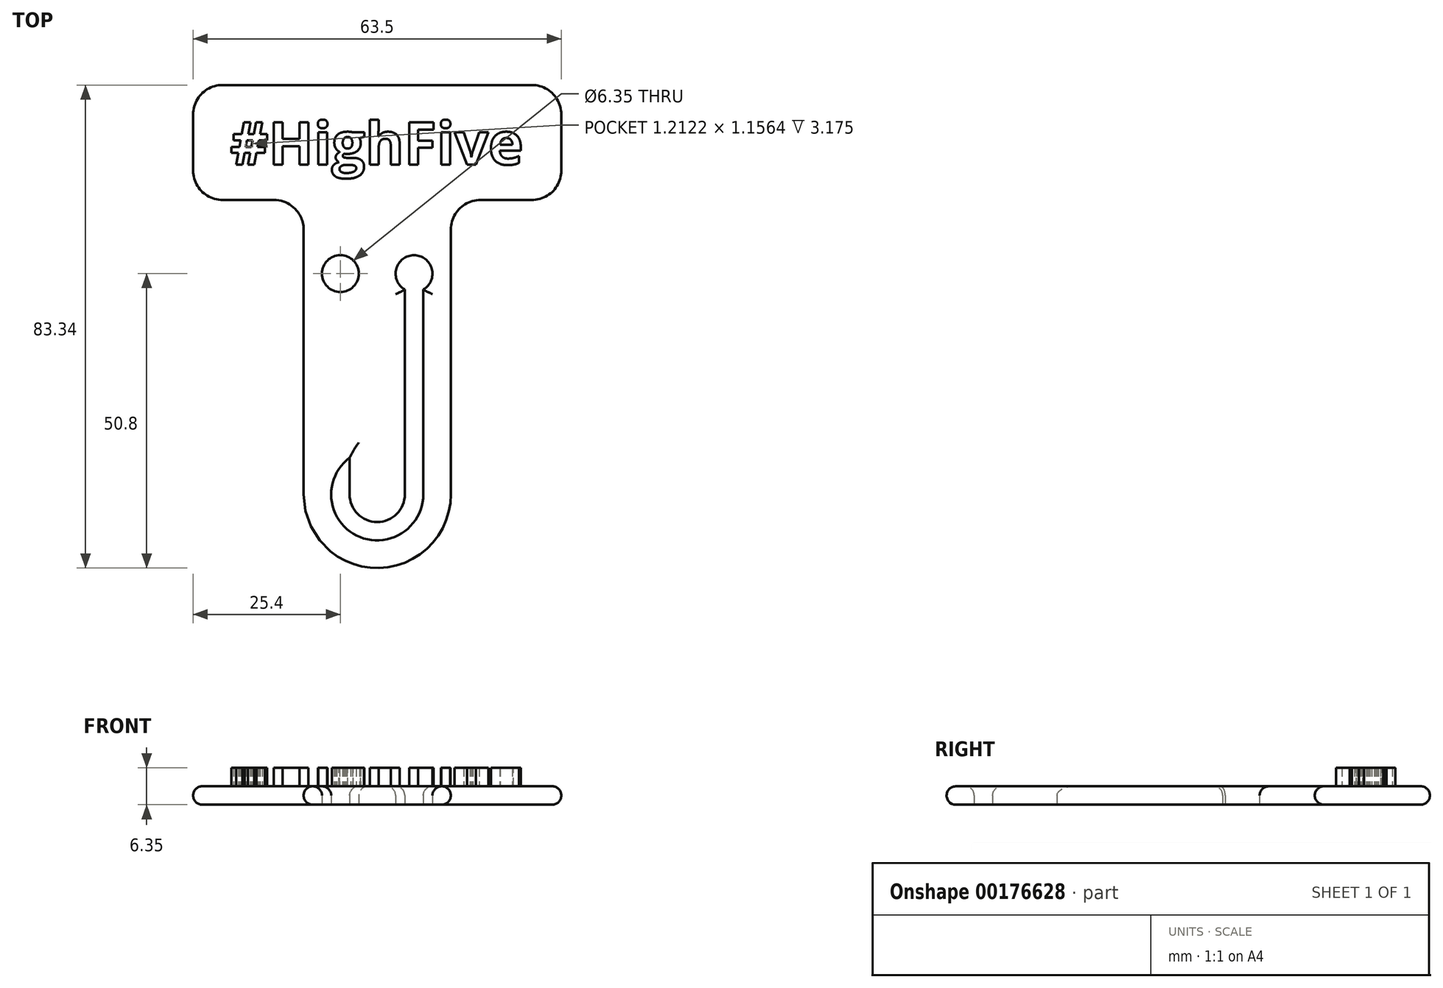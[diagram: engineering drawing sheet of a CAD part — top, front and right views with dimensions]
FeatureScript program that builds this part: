
annotation { "Feature Type Name" : "Feature", "Feature Type Description" : "" }
export const myFeature = defineFeature(function(context is Context, id is Id, definition is map)
    precondition{}
    {
        {
            var Q0;
            Q0=qCreatedBy(makeId("Top.planeOp"),FACE);
            var sketch = newSketch(context, id + "F0", { "sketchPlane" : qUnion([Q0])});
            skLineSegment(sketch, "E0", {"start": v(0, 0) * mm, "end": v(0, -50.8) * mm, "construction": true});
            skLineSegment(sketch, "E1", {"start": v(0, -50.8) * mm, "end": v(0, -63.5) * mm, "construction": true});
            skLineSegment(sketch, "E2.bottom", {"start": v(12.7, 0) * mm, "end": v(-12.7, 0) * mm});
            skLineSegment(sketch, "E2.top", {"start": v(12.7, -50.8) * mm, "end": v(-12.7, -50.8) * mm});
            skLineSegment(sketch, "E2.left", {"start": v(12.7, 0) * mm, "end": v(12.7, -50.8) * mm});
            skLineSegment(sketch, "E2.right", {"start": v(-12.7, 0) * mm, "end": v(-12.7, -50.8) * mm});
            skPoint(sketch, "E2.middle", {"position": v(0, -25.4) * mm});
            skLineSegment(sketch, "E3", {"start": v(0, 0) * mm, "end": v(0, 9.92) * mm, "construction": true});
            skLineSegment(sketch, "E4.bottom", {"start": v(31.75, 0) * mm, "end": v(-31.75, 0) * mm});
            skLineSegment(sketch, "E4.top", {"start": v(31.75, 19.84) * mm, "end": v(-31.75, 19.84) * mm});
            skLineSegment(sketch, "E4.left", {"start": v(31.75, 0) * mm, "end": v(31.75, 19.84) * mm});
            skLineSegment(sketch, "E4.right", {"start": v(-31.75, 0) * mm, "end": v(-31.75, 19.84) * mm});
            skPoint(sketch, "E4.middle", {"position": v(0, 9.92) * mm});
            skArc(sketch, "E5", {"start": v(-12.7, -50.8) * mm, "mid": v(0, -63.5) * mm, "end": v(12.7, -50.8) * mm});
            skText(sketch, "E6", { "text": "#HighFive", "fontName": "OpenSans-Bold.ttf"});
            const initialGuessF0  = {"E6": [-0.02537, 0.00611, 1, 0, 0.00735]};
            skSetInitialGuess(sketch, initialGuessF0);
            skSolve(sketch);
        }
        {
            var Q0;
            Q0=makeQuery(id+"F0.imprint","IMPRINT",FACE,{"disambiguationData":[TD([[makeQuery(id+"F0.imprint","IMPRINT",EDGE,{"derivedFrom":sQuery(id+"F0.wireOp",EDGE,"E2.top")}),1.0]])]});
            var Q1;
            Q1=makeQuery(id+"F0.imprint","IMPRINT",FACE,{"disambiguationData":[TD([[makeQuery(id+"F0.imprint","IMPRINT",EDGE,{"derivedFrom":sQuery(id+"F0.wireOp",EDGE,"E2.top")}),-1.0]])]});
            var Q2;
            Q2=makeQuery(id+"F0.imprint","IMPRINT",FACE,{"disambiguationData":[TD([[makeQuery(id+"F0.imprint","IMPRINT",EDGE,{"derivedFrom":sQuery(id+"F0.wireOp",EDGE,"E4.top")}),1.0]])]});
            var Q3;
            Q3=makeQuery(id+"F0.imprint","IMPRINT",FACE,{"disambiguationData":[TD([[makeQuery(id+"F0.imprint","IMPRINT",EDGE,{"derivedFrom":sQuery(id+"F0.wireOp",EDGE,"E6.sketch_text.stroke-82")}),1.0]])]});
            var Q4;
            Q4=makeQuery(id+"F0.imprint","IMPRINT",FACE,{"disambiguationData":[TD([[makeQuery(id+"F0.imprint","IMPRINT",EDGE,{"derivedFrom":sQuery(id+"F0.wireOp",EDGE,"E6.sketch_text.stroke-91")}),1.0]])]});
            var Q5;
            Q5=makeQuery(id+"F0.imprint","IMPRINT",FACE,{"disambiguationData":[TD([[makeQuery(id+"F0.imprint","IMPRINT",EDGE,{"derivedFrom":sQuery(id+"F0.wireOp",EDGE,"E6.sketch_text.stroke-28")}),1.0]])]});
            var Q6;
            Q6=makeQuery(id+"F0.imprint","IMPRINT",FACE,{"disambiguationData":[TD([[makeQuery(id+"F0.imprint","IMPRINT",EDGE,{"derivedFrom":sQuery(id+"F0.wireOp",EDGE,"E6.sketch_text.stroke-143")}),1.0]])]});
            extrude(context, id + "F1", {"entities" : qUnion([Q0, Q1, Q2, Q3, Q4, Q5, Q6]), "depth" : 3.17 * mm});
        }
        {
            var Q0;
            Q0=makeQuery(id+"F0.imprint","IMPRINT",FACE,{"disambiguationData":[TD([[makeQuery(id+"F0.imprint","IMPRINT",EDGE,{"derivedFrom":sQuery(id+"F0.wireOp",EDGE,"E6.sketch_text.stroke-32")}),-1.0]])]});
            var Q1;
            Q1=makeQuery(id+"F0.imprint","IMPRINT",FACE,{"disambiguationData":[TD([[makeQuery(id+"F0.imprint","IMPRINT",EDGE,{"derivedFrom":sQuery(id+"F0.wireOp",EDGE,"E6.sketch_text.stroke-0")}),-1.0]])]});
            var Q2;
            Q2=makeQuery(id+"F0.imprint","IMPRINT",FACE,{"disambiguationData":[TD([[makeQuery(id+"F0.imprint","IMPRINT",EDGE,{"derivedFrom":sQuery(id+"F0.wireOp",EDGE,"E6.sketch_text.stroke-49")}),-1.0]])]});
            var Q3;
            Q3=makeQuery(id+"F0.imprint","IMPRINT",FACE,{"disambiguationData":[TD([[makeQuery(id+"F0.imprint","IMPRINT",EDGE,{"derivedFrom":sQuery(id+"F0.wireOp",EDGE,"E6.sketch_text.stroke-53")}),-1.0]])]});
            var Q4;
            Q4=makeQuery(id+"F0.imprint","IMPRINT",FACE,{"disambiguationData":[TD([[makeQuery(id+"F0.imprint","IMPRINT",EDGE,{"derivedFrom":sQuery(id+"F0.wireOp",EDGE,"E6.sketch_text.stroke-97")}),-1.0]])]});
            var Q5;
            Q5=makeQuery(id+"F0.imprint","IMPRINT",FACE,{"disambiguationData":[TD([[makeQuery(id+"F0.imprint","IMPRINT",EDGE,{"derivedFrom":sQuery(id+"F0.wireOp",EDGE,"E6.sketch_text.stroke-114")}),-1.0]])]});
            var Q6;
            Q6=makeQuery(id+"F0.imprint","IMPRINT",FACE,{"disambiguationData":[TD([[makeQuery(id+"F0.imprint","IMPRINT",EDGE,{"derivedFrom":sQuery(id+"F0.wireOp",EDGE,"E6.sketch_text.stroke-44")}),-1.0]])]});
            var Q7;
            Q7=makeQuery(id+"F0.imprint","IMPRINT",FACE,{"disambiguationData":[TD([[makeQuery(id+"F0.imprint","IMPRINT",EDGE,{"derivedFrom":sQuery(id+"F0.wireOp",EDGE,"E6.sketch_text.stroke-124")}),-1.0]])]});
            var Q8;
            Q8=makeQuery(id+"F0.imprint","IMPRINT",FACE,{"disambiguationData":[TD([[makeQuery(id+"F0.imprint","IMPRINT",EDGE,{"derivedFrom":sQuery(id+"F0.wireOp",EDGE,"E6.sketch_text.stroke-129")}),-1.0]])]});
            var Q9;
            Q9=makeQuery(id+"F0.imprint","IMPRINT",FACE,{"disambiguationData":[TD([[makeQuery(id+"F0.imprint","IMPRINT",EDGE,{"derivedFrom":sQuery(id+"F0.wireOp",EDGE,"E6.sketch_text.stroke-133")}),-1.0]])]});
            var Q10;
            Q10=makeQuery(id+"F0.imprint","IMPRINT",FACE,{"disambiguationData":[TD([[makeQuery(id+"F0.imprint","IMPRINT",EDGE,{"derivedFrom":sQuery(id+"F0.wireOp",EDGE,"E6.sketch_text.stroke-143")}),-1.0]])]});
            extrude(context, id + "F2", {"entities" : qUnion([Q0, Q1, Q2, Q3, Q4, Q5, Q6, Q7, Q8, Q9, Q10]), "operationType" : NewBodyOperationType.ADD, "depth" : 6.35 * mm});
        }
        {
            var Q0;
            Q0=qCreatedBy(makeId("Top.planeOp"),FACE);
            var sketch = newSketch(context, id + "F3", { "sketchPlane" : qUnion([Q0])});
            skLineSegment(sketch, "E7", {"start": v(0, 0) * mm, "end": v(0, -50.8) * mm, "construction": true});
            skLineSegment(sketch, "E8", {"start": v(0, -50.8) * mm, "end": v(6.35, -50.8) * mm, "construction": true});
            skLineSegment(sketch, "E9", {"start": v(6.35, -50.8) * mm, "end": v(6.35, -12.7) * mm, "construction": true});
            skCircle(sketch, "E10", {"center": v(6.35, -12.7) * mm, "radius": 3.18 * mm});
            skCircle(sketch, "E11.MirrorC", {"center": v(-6.35, -12.7) * mm, "radius": 3.18 * mm});
            skLineSegment(sketch, "E12.MirrorCS", {"start": v(-6.35, -50.8) * mm, "end": v(-6.35, -12.7) * mm, "construction": true});
            skLineSegment(sketch, "E13.bottom", {"start": v(-4.76, -50.8) * mm, "end": v(-7.94, -50.8) * mm});
            skLineSegment(sketch, "E13.top", {"start": v(-4.76, -12.7) * mm, "end": v(-7.94, -12.7) * mm});
            skLineSegment(sketch, "E13.left", {"start": v(-4.76, -50.8) * mm, "end": v(-4.76, -12.7) * mm});
            skLineSegment(sketch, "E13.right", {"start": v(-7.94, -50.8) * mm, "end": v(-7.94, -12.7) * mm});
            skPoint(sketch, "E13.middle", {"position": v(-6.35, -31.75) * mm});
            skLineSegment(sketch, "E14.bottom", {"start": v(7.94, -50.8) * mm, "end": v(4.76, -50.8) * mm});
            skLineSegment(sketch, "E14.top", {"start": v(7.94, -12.7) * mm, "end": v(4.76, -12.7) * mm});
            skLineSegment(sketch, "E14.left", {"start": v(7.94, -50.8) * mm, "end": v(7.94, -12.7) * mm});
            skLineSegment(sketch, "E14.right", {"start": v(4.76, -50.8) * mm, "end": v(4.76, -12.7) * mm});
            skPoint(sketch, "E14.middle", {"position": v(6.35, -31.75) * mm});
            skCircle(sketch, "E15", {"center": v(0, -50.8) * mm, "radius": 4.76 * mm});
            skCircle(sketch, "E16", {"center": v(0, -50.8) * mm, "radius": 7.94 * mm});
            skSolve(sketch);
        }
        {
            var Q0;
            {var subQ5=sQuery(id+"F3.wireOp",EDGE,"E13.top");Q0=makeQuery(id+"F3.imprint","IMPRINT",FACE,{"disambiguationData":[TD([[makeQuery(id+"F3.imprint","IMPRINT",EDGE,{"derivedFrom":subQ5}),-1.0]])]});}
            var Q1;
            {var subQ5=sQuery(id+"F3.wireOp",EDGE,"E13.top");Q1=makeQuery(id+"F3.imprint","IMPRINT",FACE,{"disambiguationData":[TD([[makeQuery(id+"F3.imprint","IMPRINT",EDGE,{"derivedFrom":subQ5}),1.0]])]});}
            var Q2;
            {var subQ0=sQuery(id+"F3.wireOp",EDGE,"E13.left");var subQ1=sQuery(id+"F3.wireOp",EDGE,"E11.MirrorC");var subQ2=makeQuery(id+"F3.imprint","INTERSECT",VERTEX,{"derivedFrom":[subQ1,subQ0]});Q2=makeQuery(id+"F3.imprint","IMPRINT",FACE,{"disambiguationData":[TD([[makeQuery(id+"F3.imprint","IMPRINT",EDGE,{"disambiguationData":[TD([[subQ2,-1.0]])],"derivedFrom":subQ1}),1.0]])]});}
            var Q3;
            {var subQ0=sQuery(id+"F3.wireOp",EDGE,"E13.bottom");Q3=makeQuery(id+"F3.imprint","IMPRINT",FACE,{"disambiguationData":[TD([[makeQuery(id+"F3.imprint","IMPRINT",EDGE,{"derivedFrom":subQ0}),-1.0]])]});}
            var Q4;
            {var subQ0=sQuery(id+"F3.wireOp",EDGE,"E13.bottom");Q4=makeQuery(id+"F3.imprint","IMPRINT",FACE,{"disambiguationData":[TD([[makeQuery(id+"F3.imprint","IMPRINT",EDGE,{"derivedFrom":subQ0}),1.0]])]});}
            var Q5;
            {var subQ0=sQuery(id+"F3.wireOp",EDGE,"E14.bottom");Q5=makeQuery(id+"F3.imprint","IMPRINT",FACE,{"disambiguationData":[TD([[makeQuery(id+"F3.imprint","IMPRINT",EDGE,{"derivedFrom":subQ0}),-1.0]])]});}
            var Q6;
            {var subQ0=sQuery(id+"F3.wireOp",EDGE,"E14.left");var subQ1=sQuery(id+"F3.wireOp",EDGE,"E10");var subQ2=makeQuery(id+"F3.imprint","INTERSECT",VERTEX,{"derivedFrom":[subQ1,subQ0]});Q6=makeQuery(id+"F3.imprint","IMPRINT",FACE,{"disambiguationData":[TD([[makeQuery(id+"F3.imprint","IMPRINT",EDGE,{"disambiguationData":[TD([[subQ2,1.0]])],"derivedFrom":subQ1}),-1.0]])]});}
            var Q7;
            {var subQ5=sQuery(id+"F3.wireOp",EDGE,"E14.top");Q7=makeQuery(id+"F3.imprint","IMPRINT",FACE,{"disambiguationData":[TD([[makeQuery(id+"F3.imprint","IMPRINT",EDGE,{"derivedFrom":subQ5}),-1.0]])]});}
            var Q8;
            {var subQ5=sQuery(id+"F3.wireOp",EDGE,"E14.top");Q8=makeQuery(id+"F3.imprint","IMPRINT",FACE,{"disambiguationData":[TD([[makeQuery(id+"F3.imprint","IMPRINT",EDGE,{"derivedFrom":subQ5}),1.0]])]});}
            extrude(context, id + "F4", {"entities" : qUnion([Q0, Q1, Q2, Q3, Q4, Q5, Q6, Q7, Q8]), "operationType" : NewBodyOperationType.REMOVE, "depth" : 25.4 * mm});
        }
        {
            var Q0;
            Q0=makeQuery(id+"F1.opExtrude","SWEPT_EDGE",EDGE,{"disambiguationData":[OSD([sQuery(id+"F0.wireOp",EDGE,"E4.top"),sQuery(id+"F0.wireOp",EDGE,"E4.right")])]});
            var Q1;
            Q1=makeQuery(id+"F1.opExtrude","SWEPT_EDGE",EDGE,{"disambiguationData":[OSD([sQuery(id+"F0.wireOp",EDGE,"E4.top"),sQuery(id+"F0.wireOp",EDGE,"E4.left")])]});
            var Q2;
            Q2=makeQuery(id+"F1.opExtrude","SWEPT_EDGE",EDGE,{"disambiguationData":[OSD([sQuery(id+"F0.wireOp",EDGE,"E4.bottom"),sQuery(id+"F0.wireOp",EDGE,"E4.left")])]});
            var Q3;
            Q3=makeQuery(id+"F1.opExtrude","SWEPT_EDGE",EDGE,{"disambiguationData":[OSD([sQuery(id+"F0.wireOp",EDGE,"E4.bottom"),sQuery(id+"F0.wireOp",EDGE,"E4.right")])]});
            var Q4;
            Q4=makeQuery(id+"F1.opExtrude","SWEPT_EDGE",EDGE,{"disambiguationData":[OSD([sQuery(id+"F0.wireOp",EDGE,"E2.right"),sQuery(id+"F0.wireOp",EDGE,"E4.bottom")])]});
            var Q5;
            Q5=makeQuery(id+"F1.opExtrude","SWEPT_EDGE",EDGE,{"disambiguationData":[OSD([sQuery(id+"F0.wireOp",EDGE,"E2.left"),sQuery(id+"F0.wireOp",EDGE,"E4.bottom")])]});
            fillet(context, id + "F5", {"entities" : qUnion([Q0, Q1, Q2, Q3, Q4, Q5]), "radius" : 5.08 * mm, "tangentPropagation" : true, "allowEdgeOverflow" : false});
        }
        {
            var Q0;
            Q0=makeQuery(id+"F1.opExtrude","CAP_EDGE",EDGE,{"disambiguationData":[OSD([sQuery(id+"F0.wireOp",EDGE,"E2.left")])],"isStart":false});
            var Q1;
            {var subQ0=sQuery(id+"F0.wireOp",EDGE,"E4.bottom");Q1=makeQuery(id+"F1.opExtrude","CAP_EDGE",EDGE,{"disambiguationData":[OSD([subQ0]),TDD([makeQuery(id+"F0.imprint","IMPRINT",EDGE,{"disambiguationData":[TD([[makeQuery(id+"F0.imprint","INTERSECT",VERTEX,{"derivedFrom":[sQuery(id+"F0.wireOp",EDGE,"E2.left"),subQ0]}),1.0]])],"derivedFrom":subQ0})])],"isStart":false});}
            var Q2;
            Q2=makeQuery(id+"F1.opExtrude","CAP_EDGE",EDGE,{"disambiguationData":[OSD([sQuery(id+"F0.wireOp",EDGE,"E4.left")])],"isStart":false});
            var Q3;
            {var subQ0=sQuery(id+"F0.wireOp",EDGE,"E4.bottom");Q3=makeQuery(id+"F1.opExtrude","CAP_EDGE",EDGE,{"disambiguationData":[OSD([subQ0]),TDD([makeQuery(id+"F0.imprint","IMPRINT",EDGE,{"disambiguationData":[TD([[makeQuery(id+"F0.imprint","INTERSECT",VERTEX,{"derivedFrom":[sQuery(id+"F0.wireOp",EDGE,"E2.right"),subQ0]}),-1.0]])],"derivedFrom":subQ0})])],"isStart":false});}
            var Q4;
            Q4=makeQuery(id+"F1.opExtrude","CAP_EDGE",EDGE,{"disambiguationData":[OSD([sQuery(id+"F0.wireOp",EDGE,"E4.right")])],"isStart":false});
            var Q5;
            Q5=makeQuery(id+"F1.opExtrude","CAP_EDGE",EDGE,{"disambiguationData":[OSD([sQuery(id+"F0.wireOp",EDGE,"E4.top")])],"isStart":false});
            var Q6;
            Q6=makeQuery(id+"F4.boolean.opBoolean","INTERSECT",EDGE,{"derivedFrom":[makeQuery(id+"F1.opExtrude","CAP_FACE",FACE,{"disambiguationData":[OSD([sQuery(id+"F0.wireOp",EDGE,"E2.left"),sQuery(id+"F0.wireOp",EDGE,"E2.right"),sQuery(id+"F0.wireOp",EDGE,"E4.bottom"),sQuery(id+"F0.wireOp",EDGE,"E4.top"),sQuery(id+"F0.wireOp",EDGE,"E4.left"),sQuery(id+"F0.wireOp",EDGE,"E4.right"),sQuery(id+"F0.wireOp",EDGE,"E5"),sQuery(id+"F0.wireOp",EDGE,"E6.sketch_text.stroke-0"),sQuery(id+"F0.wireOp",EDGE,"E6.sketch_text.stroke-1"),sQuery(id+"F0.wireOp",EDGE,"E6.sketch_text.stroke-2"),sQuery(id+"F0.wireOp",EDGE,"E6.sketch_text.stroke-3"),sQuery(id+"F0.wireOp",EDGE,"E6.sketch_text.stroke-4"),sQuery(id+"F0.wireOp",EDGE,"E6.sketch_text.stroke-5"),sQuery(id+"F0.wireOp",EDGE,"E6.sketch_text.stroke-6"),sQuery(id+"F0.wireOp",EDGE,"E6.sketch_text.stroke-7"),sQuery(id+"F0.wireOp",EDGE,"E6.sketch_text.stroke-8"),sQuery(id+"F0.wireOp",EDGE,"E6.sketch_text.stroke-9"),sQuery(id+"F0.wireOp",EDGE,"E6.sketch_text.stroke-10"),sQuery(id+"F0.wireOp",EDGE,"E6.sketch_text.stroke-11"),sQuery(id+"F0.wireOp",EDGE,"E6.sketch_text.stroke-12"),sQuery(id+"F0.wireOp",EDGE,"E6.sketch_text.stroke-13"),sQuery(id+"F0.wireOp",EDGE,"E6.sketch_text.stroke-14"),sQuery(id+"F0.wireOp",EDGE,"E6.sketch_text.stroke-15"),sQuery(id+"F0.wireOp",EDGE,"E6.sketch_text.stroke-16"),sQuery(id+"F0.wireOp",EDGE,"E6.sketch_text.stroke-17"),sQuery(id+"F0.wireOp",EDGE,"E6.sketch_text.stroke-18"),sQuery(id+"F0.wireOp",EDGE,"E6.sketch_text.stroke-19"),sQuery(id+"F0.wireOp",EDGE,"E6.sketch_text.stroke-20"),sQuery(id+"F0.wireOp",EDGE,"E6.sketch_text.stroke-21"),sQuery(id+"F0.wireOp",EDGE,"E6.sketch_text.stroke-22"),sQuery(id+"F0.wireOp",EDGE,"E6.sketch_text.stroke-23"),sQuery(id+"F0.wireOp",EDGE,"E6.sketch_text.stroke-24"),sQuery(id+"F0.wireOp",EDGE,"E6.sketch_text.stroke-25"),sQuery(id+"F0.wireOp",EDGE,"E6.sketch_text.stroke-26"),sQuery(id+"F0.wireOp",EDGE,"E6.sketch_text.stroke-27"),sQuery(id+"F0.wireOp",EDGE,"E6.sketch_text.stroke-32"),sQuery(id+"F0.wireOp",EDGE,"E6.sketch_text.stroke-33"),sQuery(id+"F0.wireOp",EDGE,"E6.sketch_text.stroke-34"),sQuery(id+"F0.wireOp",EDGE,"E6.sketch_text.stroke-35"),sQuery(id+"F0.wireOp",EDGE,"E6.sketch_text.stroke-36"),sQuery(id+"F0.wireOp",EDGE,"E6.sketch_text.stroke-37"),sQuery(id+"F0.wireOp",EDGE,"E6.sketch_text.stroke-38"),sQuery(id+"F0.wireOp",EDGE,"E6.sketch_text.stroke-39"),sQuery(id+"F0.wireOp",EDGE,"E6.sketch_text.stroke-40"),sQuery(id+"F0.wireOp",EDGE,"E6.sketch_text.stroke-41"),sQuery(id+"F0.wireOp",EDGE,"E6.sketch_text.stroke-42"),sQuery(id+"F0.wireOp",EDGE,"E6.sketch_text.stroke-43"),sQuery(id+"F0.wireOp",EDGE,"E6.sketch_text.stroke-44"),sQuery(id+"F0.wireOp",EDGE,"E6.sketch_text.stroke-45"),sQuery(id+"F0.wireOp",EDGE,"E6.sketch_text.stroke-46"),sQuery(id+"F0.wireOp",EDGE,"E6.sketch_text.stroke-47"),sQuery(id+"F0.wireOp",EDGE,"E6.sketch_text.stroke-48"),sQuery(id+"F0.wireOp",EDGE,"E6.sketch_text.stroke-49"),sQuery(id+"F0.wireOp",EDGE,"E6.sketch_text.stroke-50"),sQuery(id+"F0.wireOp",EDGE,"E6.sketch_text.stroke-51"),sQuery(id+"F0.wireOp",EDGE,"E6.sketch_text.stroke-52"),sQuery(id+"F0.wireOp",EDGE,"E6.sketch_text.stroke-53"),sQuery(id+"F0.wireOp",EDGE,"E6.sketch_text.stroke-54"),sQuery(id+"F0.wireOp",EDGE,"E6.sketch_text.stroke-55"),sQuery(id+"F0.wireOp",EDGE,"E6.sketch_text.stroke-56"),sQuery(id+"F0.wireOp",EDGE,"E6.sketch_text.stroke-57"),sQuery(id+"F0.wireOp",EDGE,"E6.sketch_text.stroke-58"),sQuery(id+"F0.wireOp",EDGE,"E6.sketch_text.stroke-59"),sQuery(id+"F0.wireOp",EDGE,"E6.sketch_text.stroke-60"),sQuery(id+"F0.wireOp",EDGE,"E6.sketch_text.stroke-61"),sQuery(id+"F0.wireOp",EDGE,"E6.sketch_text.stroke-62"),sQuery(id+"F0.wireOp",EDGE,"E6.sketch_text.stroke-63"),sQuery(id+"F0.wireOp",EDGE,"E6.sketch_text.stroke-64"),sQuery(id+"F0.wireOp",EDGE,"E6.sketch_text.stroke-65"),sQuery(id+"F0.wireOp",EDGE,"E6.sketch_text.stroke-66"),sQuery(id+"F0.wireOp",EDGE,"E6.sketch_text.stroke-67"),sQuery(id+"F0.wireOp",EDGE,"E6.sketch_text.stroke-68"),sQuery(id+"F0.wireOp",EDGE,"E6.sketch_text.stroke-69"),sQuery(id+"F0.wireOp",EDGE,"E6.sketch_text.stroke-70"),sQuery(id+"F0.wireOp",EDGE,"E6.sketch_text.stroke-71"),sQuery(id+"F0.wireOp",EDGE,"E6.sketch_text.stroke-72"),sQuery(id+"F0.wireOp",EDGE,"E6.sketch_text.stroke-73"),sQuery(id+"F0.wireOp",EDGE,"E6.sketch_text.stroke-74"),sQuery(id+"F0.wireOp",EDGE,"E6.sketch_text.stroke-75"),sQuery(id+"F0.wireOp",EDGE,"E6.sketch_text.stroke-76"),sQuery(id+"F0.wireOp",EDGE,"E6.sketch_text.stroke-77"),sQuery(id+"F0.wireOp",EDGE,"E6.sketch_text.stroke-78"),sQuery(id+"F0.wireOp",EDGE,"E6.sketch_text.stroke-79"),sQuery(id+"F0.wireOp",EDGE,"E6.sketch_text.stroke-80"),sQuery(id+"F0.wireOp",EDGE,"E6.sketch_text.stroke-81"),sQuery(id+"F0.wireOp",EDGE,"E6.sketch_text.stroke-97"),sQuery(id+"F0.wireOp",EDGE,"E6.sketch_text.stroke-98"),sQuery(id+"F0.wireOp",EDGE,"E6.sketch_text.stroke-99"),sQuery(id+"F0.wireOp",EDGE,"E6.sketch_text.stroke-100"),sQuery(id+"F0.wireOp",EDGE,"E6.sketch_text.stroke-101"),sQuery(id+"F0.wireOp",EDGE,"E6.sketch_text.stroke-102"),sQuery(id+"F0.wireOp",EDGE,"E6.sketch_text.stroke-103"),sQuery(id+"F0.wireOp",EDGE,"E6.sketch_text.stroke-104"),sQuery(id+"F0.wireOp",EDGE,"E6.sketch_text.stroke-105"),sQuery(id+"F0.wireOp",EDGE,"E6.sketch_text.stroke-106"),sQuery(id+"F0.wireOp",EDGE,"E6.sketch_text.stroke-107"),sQuery(id+"F0.wireOp",EDGE,"E6.sketch_text.stroke-108"),sQuery(id+"F0.wireOp",EDGE,"E6.sketch_text.stroke-109"),sQuery(id+"F0.wireOp",EDGE,"E6.sketch_text.stroke-110"),sQuery(id+"F0.wireOp",EDGE,"E6.sketch_text.stroke-111"),sQuery(id+"F0.wireOp",EDGE,"E6.sketch_text.stroke-112"),sQuery(id+"F0.wireOp",EDGE,"E6.sketch_text.stroke-113"),sQuery(id+"F0.wireOp",EDGE,"E6.sketch_text.stroke-114"),sQuery(id+"F0.wireOp",EDGE,"E6.sketch_text.stroke-115"),sQuery(id+"F0.wireOp",EDGE,"E6.sketch_text.stroke-116"),sQuery(id+"F0.wireOp",EDGE,"E6.sketch_text.stroke-117"),sQuery(id+"F0.wireOp",EDGE,"E6.sketch_text.stroke-118"),sQuery(id+"F0.wireOp",EDGE,"E6.sketch_text.stroke-119"),sQuery(id+"F0.wireOp",EDGE,"E6.sketch_text.stroke-120"),sQuery(id+"F0.wireOp",EDGE,"E6.sketch_text.stroke-121"),sQuery(id+"F0.wireOp",EDGE,"E6.sketch_text.stroke-122"),sQuery(id+"F0.wireOp",EDGE,"E6.sketch_text.stroke-123"),sQuery(id+"F0.wireOp",EDGE,"E6.sketch_text.stroke-124"),sQuery(id+"F0.wireOp",EDGE,"E6.sketch_text.stroke-125"),sQuery(id+"F0.wireOp",EDGE,"E6.sketch_text.stroke-126"),sQuery(id+"F0.wireOp",EDGE,"E6.sketch_text.stroke-127"),sQuery(id+"F0.wireOp",EDGE,"E6.sketch_text.stroke-128"),sQuery(id+"F0.wireOp",EDGE,"E6.sketch_text.stroke-129"),sQuery(id+"F0.wireOp",EDGE,"E6.sketch_text.stroke-130"),sQuery(id+"F0.wireOp",EDGE,"E6.sketch_text.stroke-131"),sQuery(id+"F0.wireOp",EDGE,"E6.sketch_text.stroke-132"),sQuery(id+"F0.wireOp",EDGE,"E6.sketch_text.stroke-133"),sQuery(id+"F0.wireOp",EDGE,"E6.sketch_text.stroke-134"),sQuery(id+"F0.wireOp",EDGE,"E6.sketch_text.stroke-135"),sQuery(id+"F0.wireOp",EDGE,"E6.sketch_text.stroke-136"),sQuery(id+"F0.wireOp",EDGE,"E6.sketch_text.stroke-137"),sQuery(id+"F0.wireOp",EDGE,"E6.sketch_text.stroke-138"),sQuery(id+"F0.wireOp",EDGE,"E6.sketch_text.stroke-139"),sQuery(id+"F0.wireOp",EDGE,"E6.sketch_text.stroke-140"),sQuery(id+"F0.wireOp",EDGE,"E6.sketch_text.stroke-141"),sQuery(id+"F0.wireOp",EDGE,"E6.sketch_text.stroke-142"),sQuery(id+"F0.wireOp",EDGE,"E6.sketch_text.stroke-148"),sQuery(id+"F0.wireOp",EDGE,"E6.sketch_text.stroke-149"),sQuery(id+"F0.wireOp",EDGE,"E6.sketch_text.stroke-150"),sQuery(id+"F0.wireOp",EDGE,"E6.sketch_text.stroke-151"),sQuery(id+"F0.wireOp",EDGE,"E6.sketch_text.stroke-152"),sQuery(id+"F0.wireOp",EDGE,"E6.sketch_text.stroke-153"),sQuery(id+"F0.wireOp",EDGE,"E6.sketch_text.stroke-154"),sQuery(id+"F0.wireOp",EDGE,"E6.sketch_text.stroke-155"),sQuery(id+"F0.wireOp",EDGE,"E6.sketch_text.stroke-156"),sQuery(id+"F0.wireOp",EDGE,"E6.sketch_text.stroke-157"),sQuery(id+"F0.wireOp",EDGE,"E6.sketch_text.stroke-158"),sQuery(id+"F0.wireOp",EDGE,"E6.sketch_text.stroke-159"),sQuery(id+"F0.wireOp",EDGE,"E6.sketch_text.stroke-160"),sQuery(id+"F0.wireOp",EDGE,"E6.sketch_text.stroke-161"),sQuery(id+"F0.wireOp",EDGE,"E6.sketch_text.stroke-162")])],"isStart":false}),makeQuery(id+"F4.opExtrude","SWEPT_FACE",FACE,{"disambiguationData":[OSD([sQuery(id+"F3.wireOp",EDGE,"E14.left")])]})]});
            var Q7;
            Q7=makeQuery(id+"F4.boolean.opBoolean","INTERSECT",EDGE,{"derivedFrom":[makeQuery(id+"F1.opExtrude","CAP_FACE",FACE,{"disambiguationData":[OSD([sQuery(id+"F0.wireOp",EDGE,"E2.left"),sQuery(id+"F0.wireOp",EDGE,"E2.right"),sQuery(id+"F0.wireOp",EDGE,"E4.bottom"),sQuery(id+"F0.wireOp",EDGE,"E4.top"),sQuery(id+"F0.wireOp",EDGE,"E4.left"),sQuery(id+"F0.wireOp",EDGE,"E4.right"),sQuery(id+"F0.wireOp",EDGE,"E5"),sQuery(id+"F0.wireOp",EDGE,"E6.sketch_text.stroke-0"),sQuery(id+"F0.wireOp",EDGE,"E6.sketch_text.stroke-1"),sQuery(id+"F0.wireOp",EDGE,"E6.sketch_text.stroke-2"),sQuery(id+"F0.wireOp",EDGE,"E6.sketch_text.stroke-3"),sQuery(id+"F0.wireOp",EDGE,"E6.sketch_text.stroke-4"),sQuery(id+"F0.wireOp",EDGE,"E6.sketch_text.stroke-5"),sQuery(id+"F0.wireOp",EDGE,"E6.sketch_text.stroke-6"),sQuery(id+"F0.wireOp",EDGE,"E6.sketch_text.stroke-7"),sQuery(id+"F0.wireOp",EDGE,"E6.sketch_text.stroke-8"),sQuery(id+"F0.wireOp",EDGE,"E6.sketch_text.stroke-9"),sQuery(id+"F0.wireOp",EDGE,"E6.sketch_text.stroke-10"),sQuery(id+"F0.wireOp",EDGE,"E6.sketch_text.stroke-11"),sQuery(id+"F0.wireOp",EDGE,"E6.sketch_text.stroke-12"),sQuery(id+"F0.wireOp",EDGE,"E6.sketch_text.stroke-13"),sQuery(id+"F0.wireOp",EDGE,"E6.sketch_text.stroke-14"),sQuery(id+"F0.wireOp",EDGE,"E6.sketch_text.stroke-15"),sQuery(id+"F0.wireOp",EDGE,"E6.sketch_text.stroke-16"),sQuery(id+"F0.wireOp",EDGE,"E6.sketch_text.stroke-17"),sQuery(id+"F0.wireOp",EDGE,"E6.sketch_text.stroke-18"),sQuery(id+"F0.wireOp",EDGE,"E6.sketch_text.stroke-19"),sQuery(id+"F0.wireOp",EDGE,"E6.sketch_text.stroke-20"),sQuery(id+"F0.wireOp",EDGE,"E6.sketch_text.stroke-21"),sQuery(id+"F0.wireOp",EDGE,"E6.sketch_text.stroke-22"),sQuery(id+"F0.wireOp",EDGE,"E6.sketch_text.stroke-23"),sQuery(id+"F0.wireOp",EDGE,"E6.sketch_text.stroke-24"),sQuery(id+"F0.wireOp",EDGE,"E6.sketch_text.stroke-25"),sQuery(id+"F0.wireOp",EDGE,"E6.sketch_text.stroke-26"),sQuery(id+"F0.wireOp",EDGE,"E6.sketch_text.stroke-27"),sQuery(id+"F0.wireOp",EDGE,"E6.sketch_text.stroke-32"),sQuery(id+"F0.wireOp",EDGE,"E6.sketch_text.stroke-33"),sQuery(id+"F0.wireOp",EDGE,"E6.sketch_text.stroke-34"),sQuery(id+"F0.wireOp",EDGE,"E6.sketch_text.stroke-35"),sQuery(id+"F0.wireOp",EDGE,"E6.sketch_text.stroke-36"),sQuery(id+"F0.wireOp",EDGE,"E6.sketch_text.stroke-37"),sQuery(id+"F0.wireOp",EDGE,"E6.sketch_text.stroke-38"),sQuery(id+"F0.wireOp",EDGE,"E6.sketch_text.stroke-39"),sQuery(id+"F0.wireOp",EDGE,"E6.sketch_text.stroke-40"),sQuery(id+"F0.wireOp",EDGE,"E6.sketch_text.stroke-41"),sQuery(id+"F0.wireOp",EDGE,"E6.sketch_text.stroke-42"),sQuery(id+"F0.wireOp",EDGE,"E6.sketch_text.stroke-43"),sQuery(id+"F0.wireOp",EDGE,"E6.sketch_text.stroke-44"),sQuery(id+"F0.wireOp",EDGE,"E6.sketch_text.stroke-45"),sQuery(id+"F0.wireOp",EDGE,"E6.sketch_text.stroke-46"),sQuery(id+"F0.wireOp",EDGE,"E6.sketch_text.stroke-47"),sQuery(id+"F0.wireOp",EDGE,"E6.sketch_text.stroke-48"),sQuery(id+"F0.wireOp",EDGE,"E6.sketch_text.stroke-49"),sQuery(id+"F0.wireOp",EDGE,"E6.sketch_text.stroke-50"),sQuery(id+"F0.wireOp",EDGE,"E6.sketch_text.stroke-51"),sQuery(id+"F0.wireOp",EDGE,"E6.sketch_text.stroke-52"),sQuery(id+"F0.wireOp",EDGE,"E6.sketch_text.stroke-53"),sQuery(id+"F0.wireOp",EDGE,"E6.sketch_text.stroke-54"),sQuery(id+"F0.wireOp",EDGE,"E6.sketch_text.stroke-55"),sQuery(id+"F0.wireOp",EDGE,"E6.sketch_text.stroke-56"),sQuery(id+"F0.wireOp",EDGE,"E6.sketch_text.stroke-57"),sQuery(id+"F0.wireOp",EDGE,"E6.sketch_text.stroke-58"),sQuery(id+"F0.wireOp",EDGE,"E6.sketch_text.stroke-59"),sQuery(id+"F0.wireOp",EDGE,"E6.sketch_text.stroke-60"),sQuery(id+"F0.wireOp",EDGE,"E6.sketch_text.stroke-61"),sQuery(id+"F0.wireOp",EDGE,"E6.sketch_text.stroke-62"),sQuery(id+"F0.wireOp",EDGE,"E6.sketch_text.stroke-63"),sQuery(id+"F0.wireOp",EDGE,"E6.sketch_text.stroke-64"),sQuery(id+"F0.wireOp",EDGE,"E6.sketch_text.stroke-65"),sQuery(id+"F0.wireOp",EDGE,"E6.sketch_text.stroke-66"),sQuery(id+"F0.wireOp",EDGE,"E6.sketch_text.stroke-67"),sQuery(id+"F0.wireOp",EDGE,"E6.sketch_text.stroke-68"),sQuery(id+"F0.wireOp",EDGE,"E6.sketch_text.stroke-69"),sQuery(id+"F0.wireOp",EDGE,"E6.sketch_text.stroke-70"),sQuery(id+"F0.wireOp",EDGE,"E6.sketch_text.stroke-71"),sQuery(id+"F0.wireOp",EDGE,"E6.sketch_text.stroke-72"),sQuery(id+"F0.wireOp",EDGE,"E6.sketch_text.stroke-73"),sQuery(id+"F0.wireOp",EDGE,"E6.sketch_text.stroke-74"),sQuery(id+"F0.wireOp",EDGE,"E6.sketch_text.stroke-75"),sQuery(id+"F0.wireOp",EDGE,"E6.sketch_text.stroke-76"),sQuery(id+"F0.wireOp",EDGE,"E6.sketch_text.stroke-77"),sQuery(id+"F0.wireOp",EDGE,"E6.sketch_text.stroke-78"),sQuery(id+"F0.wireOp",EDGE,"E6.sketch_text.stroke-79"),sQuery(id+"F0.wireOp",EDGE,"E6.sketch_text.stroke-80"),sQuery(id+"F0.wireOp",EDGE,"E6.sketch_text.stroke-81"),sQuery(id+"F0.wireOp",EDGE,"E6.sketch_text.stroke-97"),sQuery(id+"F0.wireOp",EDGE,"E6.sketch_text.stroke-98"),sQuery(id+"F0.wireOp",EDGE,"E6.sketch_text.stroke-99"),sQuery(id+"F0.wireOp",EDGE,"E6.sketch_text.stroke-100"),sQuery(id+"F0.wireOp",EDGE,"E6.sketch_text.stroke-101"),sQuery(id+"F0.wireOp",EDGE,"E6.sketch_text.stroke-102"),sQuery(id+"F0.wireOp",EDGE,"E6.sketch_text.stroke-103"),sQuery(id+"F0.wireOp",EDGE,"E6.sketch_text.stroke-104"),sQuery(id+"F0.wireOp",EDGE,"E6.sketch_text.stroke-105"),sQuery(id+"F0.wireOp",EDGE,"E6.sketch_text.stroke-106"),sQuery(id+"F0.wireOp",EDGE,"E6.sketch_text.stroke-107"),sQuery(id+"F0.wireOp",EDGE,"E6.sketch_text.stroke-108"),sQuery(id+"F0.wireOp",EDGE,"E6.sketch_text.stroke-109"),sQuery(id+"F0.wireOp",EDGE,"E6.sketch_text.stroke-110"),sQuery(id+"F0.wireOp",EDGE,"E6.sketch_text.stroke-111"),sQuery(id+"F0.wireOp",EDGE,"E6.sketch_text.stroke-112"),sQuery(id+"F0.wireOp",EDGE,"E6.sketch_text.stroke-113"),sQuery(id+"F0.wireOp",EDGE,"E6.sketch_text.stroke-114"),sQuery(id+"F0.wireOp",EDGE,"E6.sketch_text.stroke-115"),sQuery(id+"F0.wireOp",EDGE,"E6.sketch_text.stroke-116"),sQuery(id+"F0.wireOp",EDGE,"E6.sketch_text.stroke-117"),sQuery(id+"F0.wireOp",EDGE,"E6.sketch_text.stroke-118"),sQuery(id+"F0.wireOp",EDGE,"E6.sketch_text.stroke-119"),sQuery(id+"F0.wireOp",EDGE,"E6.sketch_text.stroke-120"),sQuery(id+"F0.wireOp",EDGE,"E6.sketch_text.stroke-121"),sQuery(id+"F0.wireOp",EDGE,"E6.sketch_text.stroke-122"),sQuery(id+"F0.wireOp",EDGE,"E6.sketch_text.stroke-123"),sQuery(id+"F0.wireOp",EDGE,"E6.sketch_text.stroke-124"),sQuery(id+"F0.wireOp",EDGE,"E6.sketch_text.stroke-125"),sQuery(id+"F0.wireOp",EDGE,"E6.sketch_text.stroke-126"),sQuery(id+"F0.wireOp",EDGE,"E6.sketch_text.stroke-127"),sQuery(id+"F0.wireOp",EDGE,"E6.sketch_text.stroke-128"),sQuery(id+"F0.wireOp",EDGE,"E6.sketch_text.stroke-129"),sQuery(id+"F0.wireOp",EDGE,"E6.sketch_text.stroke-130"),sQuery(id+"F0.wireOp",EDGE,"E6.sketch_text.stroke-131"),sQuery(id+"F0.wireOp",EDGE,"E6.sketch_text.stroke-132"),sQuery(id+"F0.wireOp",EDGE,"E6.sketch_text.stroke-133"),sQuery(id+"F0.wireOp",EDGE,"E6.sketch_text.stroke-134"),sQuery(id+"F0.wireOp",EDGE,"E6.sketch_text.stroke-135"),sQuery(id+"F0.wireOp",EDGE,"E6.sketch_text.stroke-136"),sQuery(id+"F0.wireOp",EDGE,"E6.sketch_text.stroke-137"),sQuery(id+"F0.wireOp",EDGE,"E6.sketch_text.stroke-138"),sQuery(id+"F0.wireOp",EDGE,"E6.sketch_text.stroke-139"),sQuery(id+"F0.wireOp",EDGE,"E6.sketch_text.stroke-140"),sQuery(id+"F0.wireOp",EDGE,"E6.sketch_text.stroke-141"),sQuery(id+"F0.wireOp",EDGE,"E6.sketch_text.stroke-142"),sQuery(id+"F0.wireOp",EDGE,"E6.sketch_text.stroke-148"),sQuery(id+"F0.wireOp",EDGE,"E6.sketch_text.stroke-149"),sQuery(id+"F0.wireOp",EDGE,"E6.sketch_text.stroke-150"),sQuery(id+"F0.wireOp",EDGE,"E6.sketch_text.stroke-151"),sQuery(id+"F0.wireOp",EDGE,"E6.sketch_text.stroke-152"),sQuery(id+"F0.wireOp",EDGE,"E6.sketch_text.stroke-153"),sQuery(id+"F0.wireOp",EDGE,"E6.sketch_text.stroke-154"),sQuery(id+"F0.wireOp",EDGE,"E6.sketch_text.stroke-155"),sQuery(id+"F0.wireOp",EDGE,"E6.sketch_text.stroke-156"),sQuery(id+"F0.wireOp",EDGE,"E6.sketch_text.stroke-157"),sQuery(id+"F0.wireOp",EDGE,"E6.sketch_text.stroke-158"),sQuery(id+"F0.wireOp",EDGE,"E6.sketch_text.stroke-159"),sQuery(id+"F0.wireOp",EDGE,"E6.sketch_text.stroke-160"),sQuery(id+"F0.wireOp",EDGE,"E6.sketch_text.stroke-161"),sQuery(id+"F0.wireOp",EDGE,"E6.sketch_text.stroke-162")])],"isStart":false}),makeQuery(id+"F4.opExtrude","SWEPT_FACE",FACE,{"disambiguationData":[OSD([sQuery(id+"F3.wireOp",EDGE,"E10")])]})]});
            var Q8;
            Q8=makeQuery(id+"F4.boolean.opBoolean","INTERSECT",EDGE,{"derivedFrom":[makeQuery(id+"F1.opExtrude","CAP_FACE",FACE,{"disambiguationData":[OSD([sQuery(id+"F0.wireOp",EDGE,"E2.left"),sQuery(id+"F0.wireOp",EDGE,"E2.right"),sQuery(id+"F0.wireOp",EDGE,"E4.bottom"),sQuery(id+"F0.wireOp",EDGE,"E4.top"),sQuery(id+"F0.wireOp",EDGE,"E4.left"),sQuery(id+"F0.wireOp",EDGE,"E4.right"),sQuery(id+"F0.wireOp",EDGE,"E5"),sQuery(id+"F0.wireOp",EDGE,"E6.sketch_text.stroke-0"),sQuery(id+"F0.wireOp",EDGE,"E6.sketch_text.stroke-1"),sQuery(id+"F0.wireOp",EDGE,"E6.sketch_text.stroke-2"),sQuery(id+"F0.wireOp",EDGE,"E6.sketch_text.stroke-3"),sQuery(id+"F0.wireOp",EDGE,"E6.sketch_text.stroke-4"),sQuery(id+"F0.wireOp",EDGE,"E6.sketch_text.stroke-5"),sQuery(id+"F0.wireOp",EDGE,"E6.sketch_text.stroke-6"),sQuery(id+"F0.wireOp",EDGE,"E6.sketch_text.stroke-7"),sQuery(id+"F0.wireOp",EDGE,"E6.sketch_text.stroke-8"),sQuery(id+"F0.wireOp",EDGE,"E6.sketch_text.stroke-9"),sQuery(id+"F0.wireOp",EDGE,"E6.sketch_text.stroke-10"),sQuery(id+"F0.wireOp",EDGE,"E6.sketch_text.stroke-11"),sQuery(id+"F0.wireOp",EDGE,"E6.sketch_text.stroke-12"),sQuery(id+"F0.wireOp",EDGE,"E6.sketch_text.stroke-13"),sQuery(id+"F0.wireOp",EDGE,"E6.sketch_text.stroke-14"),sQuery(id+"F0.wireOp",EDGE,"E6.sketch_text.stroke-15"),sQuery(id+"F0.wireOp",EDGE,"E6.sketch_text.stroke-16"),sQuery(id+"F0.wireOp",EDGE,"E6.sketch_text.stroke-17"),sQuery(id+"F0.wireOp",EDGE,"E6.sketch_text.stroke-18"),sQuery(id+"F0.wireOp",EDGE,"E6.sketch_text.stroke-19"),sQuery(id+"F0.wireOp",EDGE,"E6.sketch_text.stroke-20"),sQuery(id+"F0.wireOp",EDGE,"E6.sketch_text.stroke-21"),sQuery(id+"F0.wireOp",EDGE,"E6.sketch_text.stroke-22"),sQuery(id+"F0.wireOp",EDGE,"E6.sketch_text.stroke-23"),sQuery(id+"F0.wireOp",EDGE,"E6.sketch_text.stroke-24"),sQuery(id+"F0.wireOp",EDGE,"E6.sketch_text.stroke-25"),sQuery(id+"F0.wireOp",EDGE,"E6.sketch_text.stroke-26"),sQuery(id+"F0.wireOp",EDGE,"E6.sketch_text.stroke-27"),sQuery(id+"F0.wireOp",EDGE,"E6.sketch_text.stroke-32"),sQuery(id+"F0.wireOp",EDGE,"E6.sketch_text.stroke-33"),sQuery(id+"F0.wireOp",EDGE,"E6.sketch_text.stroke-34"),sQuery(id+"F0.wireOp",EDGE,"E6.sketch_text.stroke-35"),sQuery(id+"F0.wireOp",EDGE,"E6.sketch_text.stroke-36"),sQuery(id+"F0.wireOp",EDGE,"E6.sketch_text.stroke-37"),sQuery(id+"F0.wireOp",EDGE,"E6.sketch_text.stroke-38"),sQuery(id+"F0.wireOp",EDGE,"E6.sketch_text.stroke-39"),sQuery(id+"F0.wireOp",EDGE,"E6.sketch_text.stroke-40"),sQuery(id+"F0.wireOp",EDGE,"E6.sketch_text.stroke-41"),sQuery(id+"F0.wireOp",EDGE,"E6.sketch_text.stroke-42"),sQuery(id+"F0.wireOp",EDGE,"E6.sketch_text.stroke-43"),sQuery(id+"F0.wireOp",EDGE,"E6.sketch_text.stroke-44"),sQuery(id+"F0.wireOp",EDGE,"E6.sketch_text.stroke-45"),sQuery(id+"F0.wireOp",EDGE,"E6.sketch_text.stroke-46"),sQuery(id+"F0.wireOp",EDGE,"E6.sketch_text.stroke-47"),sQuery(id+"F0.wireOp",EDGE,"E6.sketch_text.stroke-48"),sQuery(id+"F0.wireOp",EDGE,"E6.sketch_text.stroke-49"),sQuery(id+"F0.wireOp",EDGE,"E6.sketch_text.stroke-50"),sQuery(id+"F0.wireOp",EDGE,"E6.sketch_text.stroke-51"),sQuery(id+"F0.wireOp",EDGE,"E6.sketch_text.stroke-52"),sQuery(id+"F0.wireOp",EDGE,"E6.sketch_text.stroke-53"),sQuery(id+"F0.wireOp",EDGE,"E6.sketch_text.stroke-54"),sQuery(id+"F0.wireOp",EDGE,"E6.sketch_text.stroke-55"),sQuery(id+"F0.wireOp",EDGE,"E6.sketch_text.stroke-56"),sQuery(id+"F0.wireOp",EDGE,"E6.sketch_text.stroke-57"),sQuery(id+"F0.wireOp",EDGE,"E6.sketch_text.stroke-58"),sQuery(id+"F0.wireOp",EDGE,"E6.sketch_text.stroke-59"),sQuery(id+"F0.wireOp",EDGE,"E6.sketch_text.stroke-60"),sQuery(id+"F0.wireOp",EDGE,"E6.sketch_text.stroke-61"),sQuery(id+"F0.wireOp",EDGE,"E6.sketch_text.stroke-62"),sQuery(id+"F0.wireOp",EDGE,"E6.sketch_text.stroke-63"),sQuery(id+"F0.wireOp",EDGE,"E6.sketch_text.stroke-64"),sQuery(id+"F0.wireOp",EDGE,"E6.sketch_text.stroke-65"),sQuery(id+"F0.wireOp",EDGE,"E6.sketch_text.stroke-66"),sQuery(id+"F0.wireOp",EDGE,"E6.sketch_text.stroke-67"),sQuery(id+"F0.wireOp",EDGE,"E6.sketch_text.stroke-68"),sQuery(id+"F0.wireOp",EDGE,"E6.sketch_text.stroke-69"),sQuery(id+"F0.wireOp",EDGE,"E6.sketch_text.stroke-70"),sQuery(id+"F0.wireOp",EDGE,"E6.sketch_text.stroke-71"),sQuery(id+"F0.wireOp",EDGE,"E6.sketch_text.stroke-72"),sQuery(id+"F0.wireOp",EDGE,"E6.sketch_text.stroke-73"),sQuery(id+"F0.wireOp",EDGE,"E6.sketch_text.stroke-74"),sQuery(id+"F0.wireOp",EDGE,"E6.sketch_text.stroke-75"),sQuery(id+"F0.wireOp",EDGE,"E6.sketch_text.stroke-76"),sQuery(id+"F0.wireOp",EDGE,"E6.sketch_text.stroke-77"),sQuery(id+"F0.wireOp",EDGE,"E6.sketch_text.stroke-78"),sQuery(id+"F0.wireOp",EDGE,"E6.sketch_text.stroke-79"),sQuery(id+"F0.wireOp",EDGE,"E6.sketch_text.stroke-80"),sQuery(id+"F0.wireOp",EDGE,"E6.sketch_text.stroke-81"),sQuery(id+"F0.wireOp",EDGE,"E6.sketch_text.stroke-97"),sQuery(id+"F0.wireOp",EDGE,"E6.sketch_text.stroke-98"),sQuery(id+"F0.wireOp",EDGE,"E6.sketch_text.stroke-99"),sQuery(id+"F0.wireOp",EDGE,"E6.sketch_text.stroke-100"),sQuery(id+"F0.wireOp",EDGE,"E6.sketch_text.stroke-101"),sQuery(id+"F0.wireOp",EDGE,"E6.sketch_text.stroke-102"),sQuery(id+"F0.wireOp",EDGE,"E6.sketch_text.stroke-103"),sQuery(id+"F0.wireOp",EDGE,"E6.sketch_text.stroke-104"),sQuery(id+"F0.wireOp",EDGE,"E6.sketch_text.stroke-105"),sQuery(id+"F0.wireOp",EDGE,"E6.sketch_text.stroke-106"),sQuery(id+"F0.wireOp",EDGE,"E6.sketch_text.stroke-107"),sQuery(id+"F0.wireOp",EDGE,"E6.sketch_text.stroke-108"),sQuery(id+"F0.wireOp",EDGE,"E6.sketch_text.stroke-109"),sQuery(id+"F0.wireOp",EDGE,"E6.sketch_text.stroke-110"),sQuery(id+"F0.wireOp",EDGE,"E6.sketch_text.stroke-111"),sQuery(id+"F0.wireOp",EDGE,"E6.sketch_text.stroke-112"),sQuery(id+"F0.wireOp",EDGE,"E6.sketch_text.stroke-113"),sQuery(id+"F0.wireOp",EDGE,"E6.sketch_text.stroke-114"),sQuery(id+"F0.wireOp",EDGE,"E6.sketch_text.stroke-115"),sQuery(id+"F0.wireOp",EDGE,"E6.sketch_text.stroke-116"),sQuery(id+"F0.wireOp",EDGE,"E6.sketch_text.stroke-117"),sQuery(id+"F0.wireOp",EDGE,"E6.sketch_text.stroke-118"),sQuery(id+"F0.wireOp",EDGE,"E6.sketch_text.stroke-119"),sQuery(id+"F0.wireOp",EDGE,"E6.sketch_text.stroke-120"),sQuery(id+"F0.wireOp",EDGE,"E6.sketch_text.stroke-121"),sQuery(id+"F0.wireOp",EDGE,"E6.sketch_text.stroke-122"),sQuery(id+"F0.wireOp",EDGE,"E6.sketch_text.stroke-123"),sQuery(id+"F0.wireOp",EDGE,"E6.sketch_text.stroke-124"),sQuery(id+"F0.wireOp",EDGE,"E6.sketch_text.stroke-125"),sQuery(id+"F0.wireOp",EDGE,"E6.sketch_text.stroke-126"),sQuery(id+"F0.wireOp",EDGE,"E6.sketch_text.stroke-127"),sQuery(id+"F0.wireOp",EDGE,"E6.sketch_text.stroke-128"),sQuery(id+"F0.wireOp",EDGE,"E6.sketch_text.stroke-129"),sQuery(id+"F0.wireOp",EDGE,"E6.sketch_text.stroke-130"),sQuery(id+"F0.wireOp",EDGE,"E6.sketch_text.stroke-131"),sQuery(id+"F0.wireOp",EDGE,"E6.sketch_text.stroke-132"),sQuery(id+"F0.wireOp",EDGE,"E6.sketch_text.stroke-133"),sQuery(id+"F0.wireOp",EDGE,"E6.sketch_text.stroke-134"),sQuery(id+"F0.wireOp",EDGE,"E6.sketch_text.stroke-135"),sQuery(id+"F0.wireOp",EDGE,"E6.sketch_text.stroke-136"),sQuery(id+"F0.wireOp",EDGE,"E6.sketch_text.stroke-137"),sQuery(id+"F0.wireOp",EDGE,"E6.sketch_text.stroke-138"),sQuery(id+"F0.wireOp",EDGE,"E6.sketch_text.stroke-139"),sQuery(id+"F0.wireOp",EDGE,"E6.sketch_text.stroke-140"),sQuery(id+"F0.wireOp",EDGE,"E6.sketch_text.stroke-141"),sQuery(id+"F0.wireOp",EDGE,"E6.sketch_text.stroke-142"),sQuery(id+"F0.wireOp",EDGE,"E6.sketch_text.stroke-148"),sQuery(id+"F0.wireOp",EDGE,"E6.sketch_text.stroke-149"),sQuery(id+"F0.wireOp",EDGE,"E6.sketch_text.stroke-150"),sQuery(id+"F0.wireOp",EDGE,"E6.sketch_text.stroke-151"),sQuery(id+"F0.wireOp",EDGE,"E6.sketch_text.stroke-152"),sQuery(id+"F0.wireOp",EDGE,"E6.sketch_text.stroke-153"),sQuery(id+"F0.wireOp",EDGE,"E6.sketch_text.stroke-154"),sQuery(id+"F0.wireOp",EDGE,"E6.sketch_text.stroke-155"),sQuery(id+"F0.wireOp",EDGE,"E6.sketch_text.stroke-156"),sQuery(id+"F0.wireOp",EDGE,"E6.sketch_text.stroke-157"),sQuery(id+"F0.wireOp",EDGE,"E6.sketch_text.stroke-158"),sQuery(id+"F0.wireOp",EDGE,"E6.sketch_text.stroke-159"),sQuery(id+"F0.wireOp",EDGE,"E6.sketch_text.stroke-160"),sQuery(id+"F0.wireOp",EDGE,"E6.sketch_text.stroke-161"),sQuery(id+"F0.wireOp",EDGE,"E6.sketch_text.stroke-162")])],"isStart":false}),makeQuery(id+"F4.opExtrude","SWEPT_FACE",FACE,{"disambiguationData":[OSD([sQuery(id+"F3.wireOp",EDGE,"E14.right")])]})]});
            var Q9;
            Q9=makeQuery(id+"F4.boolean.opBoolean","INTERSECT",EDGE,{"derivedFrom":[makeQuery(id+"F1.opExtrude","CAP_FACE",FACE,{"disambiguationData":[OSD([sQuery(id+"F0.wireOp",EDGE,"E2.left"),sQuery(id+"F0.wireOp",EDGE,"E2.right"),sQuery(id+"F0.wireOp",EDGE,"E4.bottom"),sQuery(id+"F0.wireOp",EDGE,"E4.top"),sQuery(id+"F0.wireOp",EDGE,"E4.left"),sQuery(id+"F0.wireOp",EDGE,"E4.right"),sQuery(id+"F0.wireOp",EDGE,"E5"),sQuery(id+"F0.wireOp",EDGE,"E6.sketch_text.stroke-0"),sQuery(id+"F0.wireOp",EDGE,"E6.sketch_text.stroke-1"),sQuery(id+"F0.wireOp",EDGE,"E6.sketch_text.stroke-2"),sQuery(id+"F0.wireOp",EDGE,"E6.sketch_text.stroke-3"),sQuery(id+"F0.wireOp",EDGE,"E6.sketch_text.stroke-4"),sQuery(id+"F0.wireOp",EDGE,"E6.sketch_text.stroke-5"),sQuery(id+"F0.wireOp",EDGE,"E6.sketch_text.stroke-6"),sQuery(id+"F0.wireOp",EDGE,"E6.sketch_text.stroke-7"),sQuery(id+"F0.wireOp",EDGE,"E6.sketch_text.stroke-8"),sQuery(id+"F0.wireOp",EDGE,"E6.sketch_text.stroke-9"),sQuery(id+"F0.wireOp",EDGE,"E6.sketch_text.stroke-10"),sQuery(id+"F0.wireOp",EDGE,"E6.sketch_text.stroke-11"),sQuery(id+"F0.wireOp",EDGE,"E6.sketch_text.stroke-12"),sQuery(id+"F0.wireOp",EDGE,"E6.sketch_text.stroke-13"),sQuery(id+"F0.wireOp",EDGE,"E6.sketch_text.stroke-14"),sQuery(id+"F0.wireOp",EDGE,"E6.sketch_text.stroke-15"),sQuery(id+"F0.wireOp",EDGE,"E6.sketch_text.stroke-16"),sQuery(id+"F0.wireOp",EDGE,"E6.sketch_text.stroke-17"),sQuery(id+"F0.wireOp",EDGE,"E6.sketch_text.stroke-18"),sQuery(id+"F0.wireOp",EDGE,"E6.sketch_text.stroke-19"),sQuery(id+"F0.wireOp",EDGE,"E6.sketch_text.stroke-20"),sQuery(id+"F0.wireOp",EDGE,"E6.sketch_text.stroke-21"),sQuery(id+"F0.wireOp",EDGE,"E6.sketch_text.stroke-22"),sQuery(id+"F0.wireOp",EDGE,"E6.sketch_text.stroke-23"),sQuery(id+"F0.wireOp",EDGE,"E6.sketch_text.stroke-24"),sQuery(id+"F0.wireOp",EDGE,"E6.sketch_text.stroke-25"),sQuery(id+"F0.wireOp",EDGE,"E6.sketch_text.stroke-26"),sQuery(id+"F0.wireOp",EDGE,"E6.sketch_text.stroke-27"),sQuery(id+"F0.wireOp",EDGE,"E6.sketch_text.stroke-32"),sQuery(id+"F0.wireOp",EDGE,"E6.sketch_text.stroke-33"),sQuery(id+"F0.wireOp",EDGE,"E6.sketch_text.stroke-34"),sQuery(id+"F0.wireOp",EDGE,"E6.sketch_text.stroke-35"),sQuery(id+"F0.wireOp",EDGE,"E6.sketch_text.stroke-36"),sQuery(id+"F0.wireOp",EDGE,"E6.sketch_text.stroke-37"),sQuery(id+"F0.wireOp",EDGE,"E6.sketch_text.stroke-38"),sQuery(id+"F0.wireOp",EDGE,"E6.sketch_text.stroke-39"),sQuery(id+"F0.wireOp",EDGE,"E6.sketch_text.stroke-40"),sQuery(id+"F0.wireOp",EDGE,"E6.sketch_text.stroke-41"),sQuery(id+"F0.wireOp",EDGE,"E6.sketch_text.stroke-42"),sQuery(id+"F0.wireOp",EDGE,"E6.sketch_text.stroke-43"),sQuery(id+"F0.wireOp",EDGE,"E6.sketch_text.stroke-44"),sQuery(id+"F0.wireOp",EDGE,"E6.sketch_text.stroke-45"),sQuery(id+"F0.wireOp",EDGE,"E6.sketch_text.stroke-46"),sQuery(id+"F0.wireOp",EDGE,"E6.sketch_text.stroke-47"),sQuery(id+"F0.wireOp",EDGE,"E6.sketch_text.stroke-48"),sQuery(id+"F0.wireOp",EDGE,"E6.sketch_text.stroke-49"),sQuery(id+"F0.wireOp",EDGE,"E6.sketch_text.stroke-50"),sQuery(id+"F0.wireOp",EDGE,"E6.sketch_text.stroke-51"),sQuery(id+"F0.wireOp",EDGE,"E6.sketch_text.stroke-52"),sQuery(id+"F0.wireOp",EDGE,"E6.sketch_text.stroke-53"),sQuery(id+"F0.wireOp",EDGE,"E6.sketch_text.stroke-54"),sQuery(id+"F0.wireOp",EDGE,"E6.sketch_text.stroke-55"),sQuery(id+"F0.wireOp",EDGE,"E6.sketch_text.stroke-56"),sQuery(id+"F0.wireOp",EDGE,"E6.sketch_text.stroke-57"),sQuery(id+"F0.wireOp",EDGE,"E6.sketch_text.stroke-58"),sQuery(id+"F0.wireOp",EDGE,"E6.sketch_text.stroke-59"),sQuery(id+"F0.wireOp",EDGE,"E6.sketch_text.stroke-60"),sQuery(id+"F0.wireOp",EDGE,"E6.sketch_text.stroke-61"),sQuery(id+"F0.wireOp",EDGE,"E6.sketch_text.stroke-62"),sQuery(id+"F0.wireOp",EDGE,"E6.sketch_text.stroke-63"),sQuery(id+"F0.wireOp",EDGE,"E6.sketch_text.stroke-64"),sQuery(id+"F0.wireOp",EDGE,"E6.sketch_text.stroke-65"),sQuery(id+"F0.wireOp",EDGE,"E6.sketch_text.stroke-66"),sQuery(id+"F0.wireOp",EDGE,"E6.sketch_text.stroke-67"),sQuery(id+"F0.wireOp",EDGE,"E6.sketch_text.stroke-68"),sQuery(id+"F0.wireOp",EDGE,"E6.sketch_text.stroke-69"),sQuery(id+"F0.wireOp",EDGE,"E6.sketch_text.stroke-70"),sQuery(id+"F0.wireOp",EDGE,"E6.sketch_text.stroke-71"),sQuery(id+"F0.wireOp",EDGE,"E6.sketch_text.stroke-72"),sQuery(id+"F0.wireOp",EDGE,"E6.sketch_text.stroke-73"),sQuery(id+"F0.wireOp",EDGE,"E6.sketch_text.stroke-74"),sQuery(id+"F0.wireOp",EDGE,"E6.sketch_text.stroke-75"),sQuery(id+"F0.wireOp",EDGE,"E6.sketch_text.stroke-76"),sQuery(id+"F0.wireOp",EDGE,"E6.sketch_text.stroke-77"),sQuery(id+"F0.wireOp",EDGE,"E6.sketch_text.stroke-78"),sQuery(id+"F0.wireOp",EDGE,"E6.sketch_text.stroke-79"),sQuery(id+"F0.wireOp",EDGE,"E6.sketch_text.stroke-80"),sQuery(id+"F0.wireOp",EDGE,"E6.sketch_text.stroke-81"),sQuery(id+"F0.wireOp",EDGE,"E6.sketch_text.stroke-97"),sQuery(id+"F0.wireOp",EDGE,"E6.sketch_text.stroke-98"),sQuery(id+"F0.wireOp",EDGE,"E6.sketch_text.stroke-99"),sQuery(id+"F0.wireOp",EDGE,"E6.sketch_text.stroke-100"),sQuery(id+"F0.wireOp",EDGE,"E6.sketch_text.stroke-101"),sQuery(id+"F0.wireOp",EDGE,"E6.sketch_text.stroke-102"),sQuery(id+"F0.wireOp",EDGE,"E6.sketch_text.stroke-103"),sQuery(id+"F0.wireOp",EDGE,"E6.sketch_text.stroke-104"),sQuery(id+"F0.wireOp",EDGE,"E6.sketch_text.stroke-105"),sQuery(id+"F0.wireOp",EDGE,"E6.sketch_text.stroke-106"),sQuery(id+"F0.wireOp",EDGE,"E6.sketch_text.stroke-107"),sQuery(id+"F0.wireOp",EDGE,"E6.sketch_text.stroke-108"),sQuery(id+"F0.wireOp",EDGE,"E6.sketch_text.stroke-109"),sQuery(id+"F0.wireOp",EDGE,"E6.sketch_text.stroke-110"),sQuery(id+"F0.wireOp",EDGE,"E6.sketch_text.stroke-111"),sQuery(id+"F0.wireOp",EDGE,"E6.sketch_text.stroke-112"),sQuery(id+"F0.wireOp",EDGE,"E6.sketch_text.stroke-113"),sQuery(id+"F0.wireOp",EDGE,"E6.sketch_text.stroke-114"),sQuery(id+"F0.wireOp",EDGE,"E6.sketch_text.stroke-115"),sQuery(id+"F0.wireOp",EDGE,"E6.sketch_text.stroke-116"),sQuery(id+"F0.wireOp",EDGE,"E6.sketch_text.stroke-117"),sQuery(id+"F0.wireOp",EDGE,"E6.sketch_text.stroke-118"),sQuery(id+"F0.wireOp",EDGE,"E6.sketch_text.stroke-119"),sQuery(id+"F0.wireOp",EDGE,"E6.sketch_text.stroke-120"),sQuery(id+"F0.wireOp",EDGE,"E6.sketch_text.stroke-121"),sQuery(id+"F0.wireOp",EDGE,"E6.sketch_text.stroke-122"),sQuery(id+"F0.wireOp",EDGE,"E6.sketch_text.stroke-123"),sQuery(id+"F0.wireOp",EDGE,"E6.sketch_text.stroke-124"),sQuery(id+"F0.wireOp",EDGE,"E6.sketch_text.stroke-125"),sQuery(id+"F0.wireOp",EDGE,"E6.sketch_text.stroke-126"),sQuery(id+"F0.wireOp",EDGE,"E6.sketch_text.stroke-127"),sQuery(id+"F0.wireOp",EDGE,"E6.sketch_text.stroke-128"),sQuery(id+"F0.wireOp",EDGE,"E6.sketch_text.stroke-129"),sQuery(id+"F0.wireOp",EDGE,"E6.sketch_text.stroke-130"),sQuery(id+"F0.wireOp",EDGE,"E6.sketch_text.stroke-131"),sQuery(id+"F0.wireOp",EDGE,"E6.sketch_text.stroke-132"),sQuery(id+"F0.wireOp",EDGE,"E6.sketch_text.stroke-133"),sQuery(id+"F0.wireOp",EDGE,"E6.sketch_text.stroke-134"),sQuery(id+"F0.wireOp",EDGE,"E6.sketch_text.stroke-135"),sQuery(id+"F0.wireOp",EDGE,"E6.sketch_text.stroke-136"),sQuery(id+"F0.wireOp",EDGE,"E6.sketch_text.stroke-137"),sQuery(id+"F0.wireOp",EDGE,"E6.sketch_text.stroke-138"),sQuery(id+"F0.wireOp",EDGE,"E6.sketch_text.stroke-139"),sQuery(id+"F0.wireOp",EDGE,"E6.sketch_text.stroke-140"),sQuery(id+"F0.wireOp",EDGE,"E6.sketch_text.stroke-141"),sQuery(id+"F0.wireOp",EDGE,"E6.sketch_text.stroke-142"),sQuery(id+"F0.wireOp",EDGE,"E6.sketch_text.stroke-148"),sQuery(id+"F0.wireOp",EDGE,"E6.sketch_text.stroke-149"),sQuery(id+"F0.wireOp",EDGE,"E6.sketch_text.stroke-150"),sQuery(id+"F0.wireOp",EDGE,"E6.sketch_text.stroke-151"),sQuery(id+"F0.wireOp",EDGE,"E6.sketch_text.stroke-152"),sQuery(id+"F0.wireOp",EDGE,"E6.sketch_text.stroke-153"),sQuery(id+"F0.wireOp",EDGE,"E6.sketch_text.stroke-154"),sQuery(id+"F0.wireOp",EDGE,"E6.sketch_text.stroke-155"),sQuery(id+"F0.wireOp",EDGE,"E6.sketch_text.stroke-156"),sQuery(id+"F0.wireOp",EDGE,"E6.sketch_text.stroke-157"),sQuery(id+"F0.wireOp",EDGE,"E6.sketch_text.stroke-158"),sQuery(id+"F0.wireOp",EDGE,"E6.sketch_text.stroke-159"),sQuery(id+"F0.wireOp",EDGE,"E6.sketch_text.stroke-160"),sQuery(id+"F0.wireOp",EDGE,"E6.sketch_text.stroke-161"),sQuery(id+"F0.wireOp",EDGE,"E6.sketch_text.stroke-162")])],"isStart":false}),makeQuery(id+"F4.opExtrude","SWEPT_FACE",FACE,{"disambiguationData":[OSD([sQuery(id+"F3.wireOp",EDGE,"E11.MirrorC")])]})]});
            var Q10;
            Q10=makeQuery(id+"F1.opExtrude","CAP_EDGE",EDGE,{"disambiguationData":[OSD([sQuery(id+"F0.wireOp",EDGE,"E4.top")])],"isStart":true});
            var Q11;
            Q11=makeQuery(id+"F1.opExtrude","CAP_EDGE",EDGE,{"disambiguationData":[OSD([sQuery(id+"F0.wireOp",EDGE,"E4.left")])],"isStart":true});
            var Q12;
            {var subQ0=sQuery(id+"F0.wireOp",EDGE,"E4.bottom");Q12=makeQuery(id+"F1.opExtrude","CAP_EDGE",EDGE,{"disambiguationData":[OSD([subQ0]),TDD([makeQuery(id+"F0.imprint","IMPRINT",EDGE,{"disambiguationData":[TD([[makeQuery(id+"F0.imprint","INTERSECT",VERTEX,{"derivedFrom":[sQuery(id+"F0.wireOp",EDGE,"E2.left"),subQ0]}),1.0]])],"derivedFrom":subQ0})])],"isStart":true});}
            var Q13;
            {var subQ0=sQuery(id+"F0.wireOp",EDGE,"E4.bottom");Q13=makeQuery(id+"F1.opExtrude","CAP_EDGE",EDGE,{"disambiguationData":[OSD([subQ0]),TDD([makeQuery(id+"F0.imprint","IMPRINT",EDGE,{"disambiguationData":[TD([[makeQuery(id+"F0.imprint","INTERSECT",VERTEX,{"derivedFrom":[sQuery(id+"F0.wireOp",EDGE,"E2.right"),subQ0]}),-1.0]])],"derivedFrom":subQ0})])],"isStart":true});}
            var Q14;
            Q14=makeQuery(id+"F1.opExtrude","CAP_EDGE",EDGE,{"disambiguationData":[OSD([sQuery(id+"F0.wireOp",EDGE,"E4.right")])],"isStart":true});
            var Q15;
            Q15=makeQuery(id+"F1.opExtrude","CAP_EDGE",EDGE,{"disambiguationData":[OSD([sQuery(id+"F0.wireOp",EDGE,"E2.right")])],"isStart":true});
            var Q16;
            Q16=makeQuery(id+"F4.boolean.opBoolean","COPY",EDGE,{"derivedFrom":makeQuery(id+"F4.opExtrude","CAP_EDGE",EDGE,{"disambiguationData":[OSD([sQuery(id+"F3.wireOp",EDGE,"E15")])],"isStart":true})});
            var Q17;
            Q17=makeQuery(id+"F4.boolean.opBoolean","COPY",EDGE,{"derivedFrom":makeQuery(id+"F4.opExtrude","CAP_EDGE",EDGE,{"disambiguationData":[OSD([sQuery(id+"F3.wireOp",EDGE,"E11.MirrorC")])],"isStart":true})});
            var Q18;
            Q18=makeQuery(id+"F4.boolean.opBoolean","COPY",EDGE,{"derivedFrom":makeQuery(id+"F4.opExtrude","CAP_EDGE",EDGE,{"disambiguationData":[OSD([sQuery(id+"F3.wireOp",EDGE,"E10")])],"isStart":true})});
            var Q19;
            Q19=makeQuery(id+"F4.boolean.opBoolean","COPY",EDGE,{"derivedFrom":makeQuery(id+"F4.opExtrude","CAP_EDGE",EDGE,{"disambiguationData":[OSD([sQuery(id+"F3.wireOp",EDGE,"E14.left")])],"isStart":true})});
            fillet(context, id + "F6", {"entities" : qUnion([Q0, Q1, Q2, Q3, Q4, Q5, Q6, Q7, Q8, Q9, Q10, Q11, Q12, Q13, Q14, Q15, Q16, Q17, Q18, Q19]), "radius" : 1.59 * mm, "tangentPropagation" : true, "allowEdgeOverflow" : false});
        }
    });
